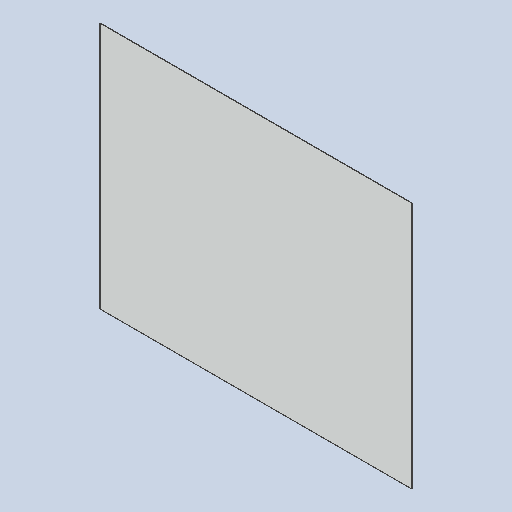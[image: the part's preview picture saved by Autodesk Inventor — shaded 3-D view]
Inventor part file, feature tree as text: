
AUTODESK INVENTOR PART (.ipt)
format: ipt  version: 2023 (Build 270158000, 158)  size: 88,064 bytes
history: native  units: mm
features: extrude x1, sketch x1
ambient origin geometry x8: Origin, YZ Plane, XZ Plane, XY Plane, X Axis, Y Axis, Z Axis, Center Point
bodies: Solid1 (feature_tree)
feature tree (2):
  extrude  "Extrusion1"  Depth=1160.0mm
  sketch  "Sketch1"  dims[d0=1460.0mm d1=1160.0mm d2=2.0mm d3=0.0mm]
